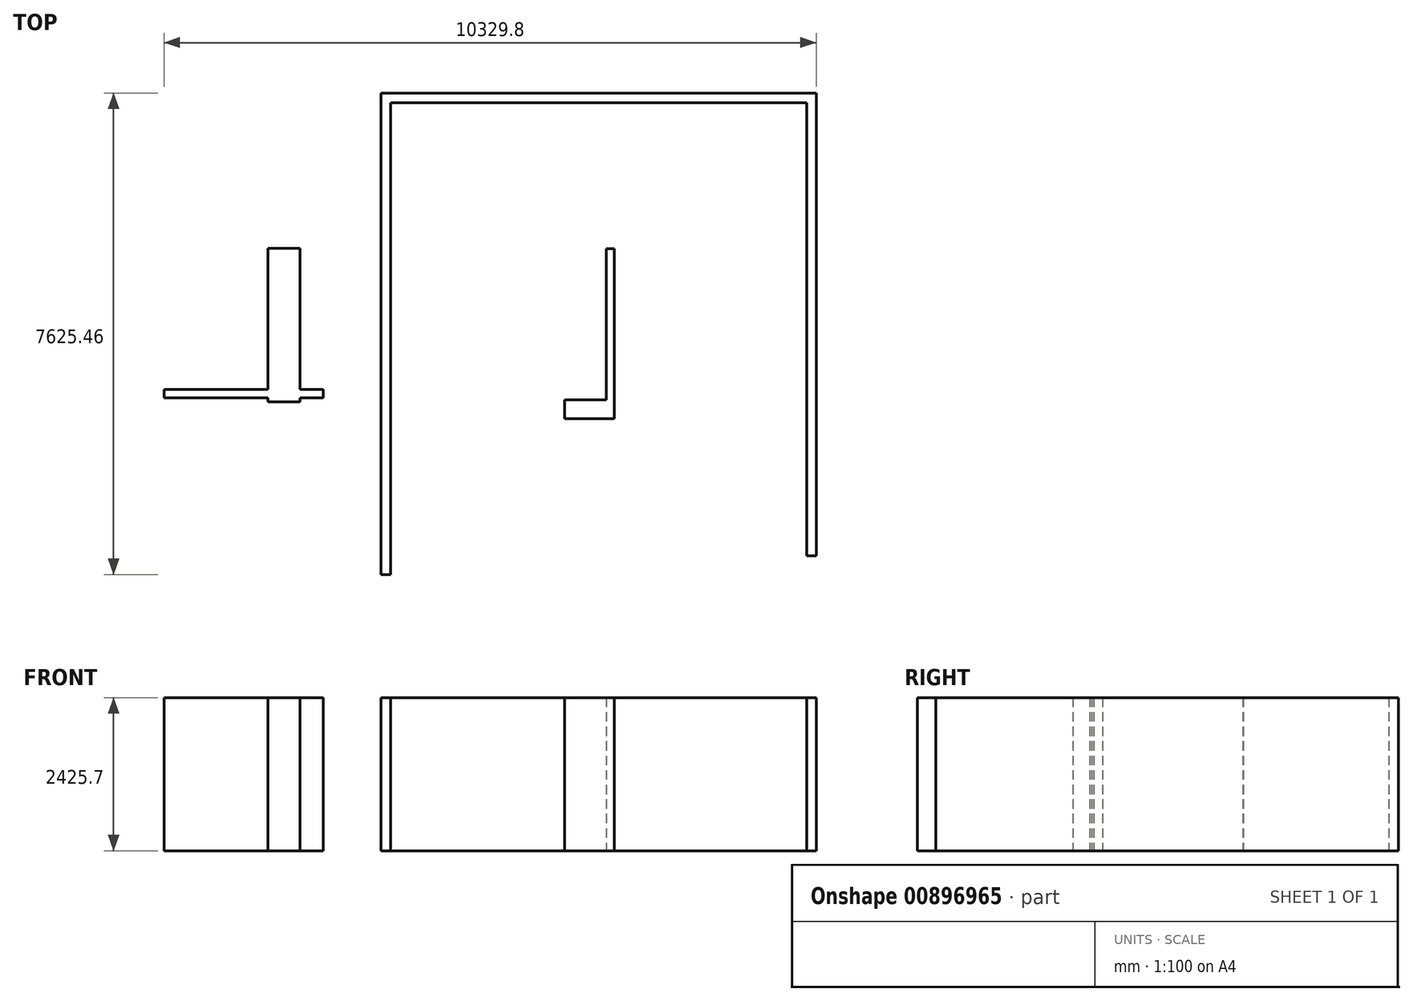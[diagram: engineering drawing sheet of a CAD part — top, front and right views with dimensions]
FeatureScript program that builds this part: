
annotation { "Feature Type Name" : "Feature", "Feature Type Description" : "" }
export const myFeature = defineFeature(function(context is Context, id is Id, definition is map)
    precondition{}
    {
        {
            var Q0;
            Q0=qCreatedBy(makeId("Top.planeOp"),FACE);
            var sketch = newSketch(context, id + "F0", { "sketchPlane" : qUnion([Q0])});
            skLineSegment(sketch, "E0", {"start": v(0, 0) * mm, "end": v(0, 2311.4) * mm, "construction": true});
            skLineSegment(sketch, "E1", {"start": v(3048, 2311.4) * mm, "end": v(0, 2311.4) * mm});
            skLineSegment(sketch, "E2", {"start": v(3048, -3784.6) * mm, "end": v(3048, 2311.4) * mm});
            skLineSegment(sketch, "E3.bottom", {"start": v(0, 0) * mm, "end": v(-127, 0) * mm});
            skLineSegment(sketch, "E3.left", {"start": v(0, 0) * mm, "end": v(0, -2692.4) * mm});
            skLineSegment(sketch, "E4.1", {"start": v(-127, 0) * mm, "end": v(-127, -2393.95) * mm});
            skLineSegment(sketch, "E5", {"start": v(0, -2692.4) * mm, "end": v(-787.4, -2692.4) * mm});
            skLineSegment(sketch, "E6", {"start": v(-787.4, -2692.4) * mm, "end": v(-787.4, -2393.95) * mm});
            skLineSegment(sketch, "E7", {"start": v(-787.4, -2393.95) * mm, "end": v(-127, -2393.95) * mm});
            skSolve(sketch);
        }
        {
            var Q0;
            Q0 = qSketchRegion(id + "F0", true);
            extrude(context, id + "F1", {"entities" : qUnion([Q0]), "depth" : 2425.7 * mm, "offsetDistance" : 25.4 * mm});
        }
        {
            var Q0;
            Q0=qCreatedBy(makeId("Top.planeOp"),FACE);
            var sketch = newSketch(context, id + "F2", { "sketchPlane" : qUnion([Q0])});
            skLineSegment(sketch, "E8", {"start": v(3048, -4868.6) * mm, "end": v(3048, 2311.4) * mm});
            skLineSegment(sketch, "E9", {"start": v(3048, 2311.4) * mm, "end": v(-3693.56, 2311.4) * mm});
            skLineSegment(sketch, "E10", {"start": v(-3693.56, 2311.4) * mm, "end": v(-3693.56, 2463.8) * mm});
            skLineSegment(sketch, "E11", {"start": v(-3693.56, 2463.8) * mm, "end": v(3200.4, 2463.8) * mm});
            skLineSegment(sketch, "E12", {"start": v(3200.4, 2463.8) * mm, "end": v(3200.4, -4868.6) * mm});
            skLineSegment(sketch, "E13", {"start": v(3200.4, -4868.6) * mm, "end": v(3048, -4868.6) * mm});
            skLineSegment(sketch, "E14.bottom", {"start": v(-3543.38, -5161.66) * mm, "end": v(-3693.56, -5161.66) * mm});
            skLineSegment(sketch, "E14.top", {"start": v(-3543.38, 2311.4) * mm, "end": v(-3693.56, 2311.4) * mm});
            skLineSegment(sketch, "E14.left", {"start": v(-3543.38, -5161.66) * mm, "end": v(-3543.38, 2311.4) * mm});
            skLineSegment(sketch, "E14.right", {"start": v(-3693.56, -5161.66) * mm, "end": v(-3693.56, 2311.4) * mm});
            skLineSegment(sketch, "E15.bottom", {"start": v(-4973.9, 3.2) * mm, "end": v(-5482.9, 3.2) * mm});
            skLineSegment(sketch, "E15.top", {"start": v(-4973.9, -2428.8) * mm, "end": v(-5482.9, -2428.8) * mm});
            skLineSegment(sketch, "E15.left", {"start": v(-4973.9, -2428.8) * mm, "end": v(-4973.9, 3.2) * mm});
            skLineSegment(sketch, "E15.right", {"start": v(-5482.9, -2428.8) * mm, "end": v(-5482.9, 3.2) * mm});
            skLineSegment(sketch, "E16.bottom", {"start": v(-4973.9, 3.2) * mm, "end": v(-3693.56, 3.2) * mm});
            skLineSegment(sketch, "E16.top", {"start": v(-4973.9, 3.2) * mm, "end": v(-3693.56, 3.2) * mm});
            skLineSegment(sketch, "E16.left", {"start": v(-4973.9, 3.2) * mm, "end": v(-4973.9, 3.2) * mm});
            skLineSegment(sketch, "E16.right", {"start": v(-3693.56, 3.2) * mm, "end": v(-3693.56, 3.2) * mm});
            skLineSegment(sketch, "E17.bottom", {"start": v(-4610.7, -2228.05) * mm, "end": v(-7129.4, -2228.05) * mm});
            skLineSegment(sketch, "E17.top", {"start": v(-4610.7, -2364.85) * mm, "end": v(-7129.4, -2364.85) * mm});
            skLineSegment(sketch, "E17.left", {"start": v(-4610.7, -2228.05) * mm, "end": v(-4610.7, -2364.85) * mm});
            skLineSegment(sketch, "E17.right", {"start": v(-7129.4, -2228.05) * mm, "end": v(-7129.4, -2364.85) * mm});
            skSolve(sketch);
        }
        {
            var Q0;
            Q0 = qSketchRegion(id + "F2", true);
            extrude(context, id + "F3", {"entities" : qUnion([Q0]), "depth" : 2425.7 * mm, "offsetDistance" : 25.4 * mm});
        }
    });
